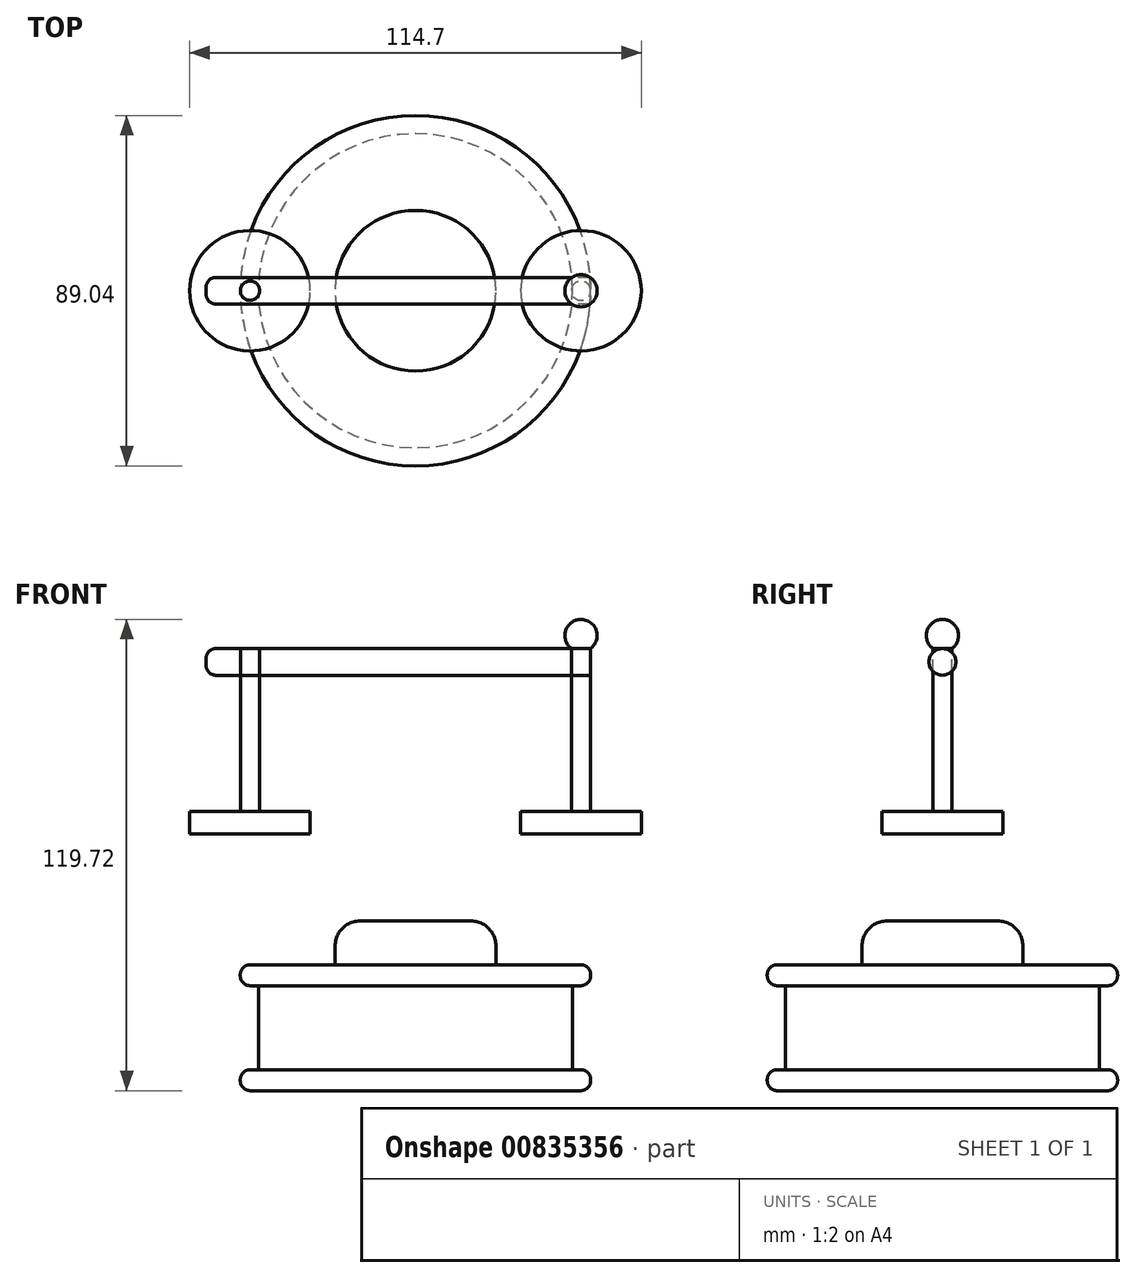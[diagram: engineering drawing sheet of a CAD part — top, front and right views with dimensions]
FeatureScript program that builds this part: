
annotation { "Feature Type Name" : "Feature", "Feature Type Description" : "" }
export const myFeature = defineFeature(function(context is Context, id is Id, definition is map)
    precondition{}
    {
        {
            var Q0;
            Q0=qCreatedBy(makeId("Front.planeOp"),FACE);
            var sketch = newSketch(context, id + "F0", { "sketchPlane" : qUnion([Q0])});
            skPoint(sketch, "E0.middle", {"position": v(0, -51.8) * mm});
            skLineSegment(sketch, "E1.bottom", {"start": v(41.98, -41.46) * mm, "end": v(-41.98, -41.46) * mm});
            skLineSegment(sketch, "E1.top", {"start": v(41.98, -36.1) * mm, "end": v(-41.98, -36.1) * mm});
            skLineSegment(sketch, "E1.left", {"start": v(44.52, -38.92) * mm, "end": v(44.52, -38.64) * mm});
            skLineSegment(sketch, "E1.right", {"start": v(-44.52, -38.92) * mm, "end": v(-44.52, -38.64) * mm});
            skPoint(sketch, "E1.middle", {"position": v(0, -38.78) * mm});
            skLineSegment(sketch, "E2.bottom", {"start": v(41.98, -68.12) * mm, "end": v(-41.98, -68.12) * mm});
            skLineSegment(sketch, "E2.top", {"start": v(41.98, -62.77) * mm, "end": v(-41.98, -62.77) * mm});
            skLineSegment(sketch, "E2.left", {"start": v(44.52, -65.58) * mm, "end": v(44.52, -65.31) * mm});
            skLineSegment(sketch, "E2.right", {"start": v(-44.52, -65.58) * mm, "end": v(-44.52, -65.31) * mm});
            skPoint(sketch, "E2.middle", {"position": v(0, -65.45) * mm});
            skLineSegment(sketch, "E3.bottom", {"start": v(20.42, -36.1) * mm, "end": v(-20.42, -36.1) * mm});
            skLineSegment(sketch, "E3.top", {"start": v(14.07, -25.01) * mm, "end": v(-14.07, -25.01) * mm});
            skLineSegment(sketch, "E3.left", {"start": v(20.42, -36.1) * mm, "end": v(20.42, -31.36) * mm});
            skLineSegment(sketch, "E3.right", {"start": v(-20.42, -36.1) * mm, "end": v(-20.42, -31.36) * mm});
            skPoint(sketch, "E3.middle", {"position": v(0, -30.56) * mm});
            skLineSegment(sketch, "E4.bottom", {"start": v(5.32, -25.01) * mm, "end": v(-5.32, -25.01) * mm});
            skLineSegment(sketch, "E4.top", {"start": v(5.32, 52.09) * mm, "end": v(-5.32, 52.09) * mm});
            skLineSegment(sketch, "E4.left", {"start": v(5.32, -25.01) * mm, "end": v(5.32, 52.09) * mm});
            skLineSegment(sketch, "E4.right", {"start": v(-5.32, -25.01) * mm, "end": v(-5.32, 52.09) * mm});
            skPoint(sketch, "E4.middle", {"position": v(0, 13.54) * mm});
            skArc(sketch, "E5", {"start": v(5.32, 52.09) * mm, "mid": v(0, 66.73) * mm, "end": v(-5.32, 52.09) * mm});
            skLineSegment(sketch, "E6.bottom", {"start": v(-5.32, 44.22) * mm, "end": v(-50.66, 44.22) * mm});
            skLineSegment(sketch, "E6.top", {"start": v(-5.32, 37.42) * mm, "end": v(-50.66, 37.42) * mm});
            skLineSegment(sketch, "E6.left", {"start": v(-5.32, 44.22) * mm, "end": v(-5.32, 37.42) * mm});
            skLineSegment(sketch, "E6.right", {"start": v(-53.2, 41.68) * mm, "end": v(-53.2, 39.96) * mm});
            skPoint(sketch, "E7.visualSharp", {"position": v(-44.52, -36.1) * mm});
            skArc(sketch, "E7.filletArc", {"start": v(-41.98, -36.1) * mm, "mid": v(-43.78, -36.85) * mm, "end": v(-44.52, -38.64) * mm});
            skPoint(sketch, "E8.visualSharp", {"position": v(-44.52, -41.46) * mm});
            skArc(sketch, "E8.filletArc", {"start": v(-44.52, -38.92) * mm, "mid": v(-43.78, -40.71) * mm, "end": v(-41.98, -41.46) * mm});
            skPoint(sketch, "E9.visualSharp", {"position": v(44.52, -36.1) * mm});
            skArc(sketch, "E9.filletArc", {"start": v(44.52, -38.64) * mm, "mid": v(43.78, -36.85) * mm, "end": v(41.98, -36.1) * mm});
            skPoint(sketch, "E10.visualSharp", {"position": v(44.52, -41.46) * mm});
            skArc(sketch, "E10.filletArc", {"start": v(41.98, -41.46) * mm, "mid": v(43.78, -40.71) * mm, "end": v(44.52, -38.92) * mm});
            skPoint(sketch, "E11.visualSharp", {"position": v(44.52, -62.77) * mm});
            skArc(sketch, "E11.filletArc", {"start": v(44.52, -65.31) * mm, "mid": v(43.78, -63.52) * mm, "end": v(41.98, -62.77) * mm});
            skPoint(sketch, "E12.visualSharp", {"position": v(44.52, -68.12) * mm});
            skArc(sketch, "E12.filletArc", {"start": v(41.98, -68.12) * mm, "mid": v(43.78, -67.38) * mm, "end": v(44.52, -65.58) * mm});
            skPoint(sketch, "E13.visualSharp", {"position": v(-44.52, -68.12) * mm});
            skArc(sketch, "E13.filletArc", {"start": v(-44.52, -65.58) * mm, "mid": v(-43.78, -67.38) * mm, "end": v(-41.98, -68.12) * mm});
            skPoint(sketch, "E14.visualSharp", {"position": v(-44.52, -62.77) * mm});
            skArc(sketch, "E14.filletArc", {"start": v(-41.98, -62.77) * mm, "mid": v(-43.78, -63.52) * mm, "end": v(-44.52, -65.31) * mm});
            skPoint(sketch, "E15.visualSharp", {"position": v(-53.2, 44.22) * mm});
            skArc(sketch, "E15.filletArc", {"start": v(-50.66, 44.22) * mm, "mid": v(-52.46, 43.48) * mm, "end": v(-53.2, 41.68) * mm});
            skPoint(sketch, "E16.visualSharp", {"position": v(-53.2, 37.42) * mm});
            skArc(sketch, "E16.filletArc", {"start": v(-53.2, 39.96) * mm, "mid": v(-52.46, 38.16) * mm, "end": v(-50.66, 37.42) * mm});
            skLineSegment(sketch, "E17.bottom", {"start": v(-44.5, 44.22) * mm, "end": v(-39.6, 44.22) * mm});
            skLineSegment(sketch, "E17.top", {"start": v(-44.5, 2.86) * mm, "end": v(-39.6, 2.86) * mm});
            skLineSegment(sketch, "E17.left", {"start": v(-44.5, 44.22) * mm, "end": v(-44.5, 2.86) * mm});
            skLineSegment(sketch, "E17.right", {"start": v(-39.6, 44.22) * mm, "end": v(-39.6, 2.86) * mm});
            skArc(sketch, "E18", {"start": v(-39.6, 44.22) * mm, "mid": v(-42.05, 51.6) * mm, "end": v(-44.5, 44.22) * mm});
            skLineSegment(sketch, "E19.bottom", {"start": v(-39.6, 2.86) * mm, "end": v(-44.5, 2.86) * mm});
            skLineSegment(sketch, "E19.top", {"start": v(-39.6, 2.86) * mm, "end": v(-44.5, 2.86) * mm});
            skLineSegment(sketch, "E19.left", {"start": v(-39.6, 2.86) * mm, "end": v(-39.6, 2.86) * mm});
            skLineSegment(sketch, "E19.right", {"start": v(-44.5, 2.86) * mm, "end": v(-44.5, 2.86) * mm});
            skPoint(sketch, "E19.middle", {"position": v(-42.05, 2.86) * mm});
            skLineSegment(sketch, "E20.bottom", {"start": v(-26.74, -2.83) * mm, "end": v(-57.35, -2.83) * mm});
            skLineSegment(sketch, "E20.top", {"start": v(-26.74, 2.83) * mm, "end": v(-57.35, 2.83) * mm});
            skLineSegment(sketch, "E20.left", {"start": v(-26.74, -2.83) * mm, "end": v(-26.74, 2.83) * mm});
            skLineSegment(sketch, "E20.right", {"start": v(-57.35, -2.83) * mm, "end": v(-57.35, 2.83) * mm});
            skPoint(sketch, "E20.middle", {"position": v(-42.05, 0) * mm});
            skLineSegment(sketch, "E21", {"start": v(0, -65.45) * mm, "end": v(0, 58.45) * mm});
            skLineSegment(sketch, "E22", {"start": v(0, -65.45) * mm, "end": v(0, -68.12) * mm});
            skLineSegment(sketch, "E23", {"start": v(0, 58.45) * mm, "end": v(0, 66.73) * mm});
            skLineSegment(sketch, "E24", {"start": v(-42.05, 0) * mm, "end": v(-42.05, 47.5) * mm});
            skLineSegment(sketch, "E25", {"start": v(-42.05, 0) * mm, "end": v(-42.05, -2.83) * mm});
            skLineSegment(sketch, "E26", {"start": v(-42.05, 47.5) * mm, "end": v(-42.05, 51.6) * mm});
            skArc(sketch, "E27.MirrorCS", {"start": v(39.6, 44.22) * mm, "mid": v(42.05, 51.6) * mm, "end": v(44.5, 44.22) * mm});
            skLineSegment(sketch, "E28.MirrorCS", {"start": v(5.32, 44.22) * mm, "end": v(50.66, 44.22) * mm});
            skLineSegment(sketch, "E29.MirrorCS", {"start": v(5.32, 37.42) * mm, "end": v(50.66, 37.42) * mm});
            skLineSegment(sketch, "E30.MirrorCS", {"start": v(39.6, 44.22) * mm, "end": v(39.6, 2.86) * mm});
            skLineSegment(sketch, "E31.MirrorCS", {"start": v(44.5, 44.22) * mm, "end": v(44.5, 2.86) * mm});
            skLineSegment(sketch, "E32.MirrorCS", {"start": v(26.74, 2.83) * mm, "end": v(57.35, 2.83) * mm});
            skLineSegment(sketch, "E33.MirrorCS", {"start": v(26.74, -2.83) * mm, "end": v(57.35, -2.83) * mm});
            skLineSegment(sketch, "E34.MirrorCS", {"start": v(57.35, -2.83) * mm, "end": v(57.35, 2.83) * mm});
            skLineSegment(sketch, "E35.MirrorCS", {"start": v(26.74, -2.83) * mm, "end": v(26.74, 2.83) * mm});
            skPoint(sketch, "E36.MirrorP", {"position": v(53.2, 44.22) * mm});
            skArc(sketch, "E37.MirrorCS", {"start": v(53.2, 39.96) * mm, "mid": v(52.46, 38.16) * mm, "end": v(50.66, 37.42) * mm});
            skLineSegment(sketch, "E38.MirrorCS", {"start": v(53.2, 41.68) * mm, "end": v(53.2, 39.96) * mm});
            skArc(sketch, "E39.MirrorCS", {"start": v(50.66, 44.22) * mm, "mid": v(52.46, 43.48) * mm, "end": v(53.2, 41.68) * mm});
            skPoint(sketch, "E40.visualSharp", {"position": v(-20.42, -25.01) * mm});
            skArc(sketch, "E40.filletArc", {"start": v(-14.07, -25.01) * mm, "mid": v(-18.56, -26.87) * mm, "end": v(-20.42, -31.36) * mm});
            skPoint(sketch, "E41.visualSharp", {"position": v(20.42, -25.01) * mm});
            skArc(sketch, "E41.filletArc", {"start": v(20.42, -31.36) * mm, "mid": v(18.56, -26.87) * mm, "end": v(14.07, -25.01) * mm});
            skLineSegment(sketch, "E42", {"start": v(0, 66.73) * mm, "end": v(0, -68.12) * mm});
            skLineSegment(sketch, "E43", {"start": v(-42.05, 51.6) * mm, "end": v(-42.05, -2.83) * mm});
            skLineSegment(sketch, "E44", {"start": v(-53.2, 40.82) * mm, "end": v(53.2, 40.82) * mm});
            skLineSegment(sketch, "E45", {"start": v(39.6, 2.86) * mm, "end": v(39.6, 2.83) * mm});
            skLineSegment(sketch, "E46", {"start": v(44.5, 2.86) * mm, "end": v(44.5, 2.83) * mm});
            skPoint(sketch, "E47.orphan", {"position": v(42.05, 0) * mm});
            skPoint(sketch, "E48.orphan", {"position": v(42.05, 51.6) * mm});
            skPoint(sketch, "E49.trimOffspring.end.orphan", {"position": v(42.05, -2.83) * mm});
            skLineSegment(sketch, "E50", {"start": v(42.05, 51.6) * mm, "end": v(42.05, -2.83) * mm});
            skLineSegment(sketch, "E51", {"start": v(5.32, 44.22) * mm, "end": v(-5.32, 44.22) * mm});
            skLineSegment(sketch, "E52", {"start": v(5.32, 37.42) * mm, "end": v(-5.32, 37.42) * mm});
            skPoint(sketch, "E53.MirrorCS.end.orphan", {"position": v(-57.35, -2.83) * mm});
            skPoint(sketch, "E53.MirrorCS.start.orphan", {"position": v(-26.74, -2.83) * mm});
            skPoint(sketch, "E54.orphan", {"position": v(-45.31, -62.14) * mm});
            skPoint(sketch, "E0.bottom.start.orphan", {"position": v(45.31, -62.14) * mm});
            skPoint(sketch, "E55.trimOffspring.end.orphan", {"position": v(-45.31, -41.46) * mm});
            skPoint(sketch, "E0.top.start.orphan", {"position": v(45.31, -41.46) * mm});
            skLineSegment(sketch, "E56.bottom", {"start": v(-39.91, -62.77) * mm, "end": v(39.91, -62.77) * mm});
            skLineSegment(sketch, "E56.left", {"start": v(-39.91, -62.77) * mm, "end": v(-39.91, -41.46) * mm});
            skLineSegment(sketch, "E56.right", {"start": v(39.91, -62.77) * mm, "end": v(39.91, -41.46) * mm});
            skPoint(sketch, "E57.orphan", {"position": v(39.91, -40.82) * mm});
            skPoint(sketch, "E58.orphan", {"position": v(-39.91, -40.82) * mm});
            skSolve(sketch);
        }
        {
            var Q0;
            {var subQ0=sQuery(id+"F0.wireOp",EDGE,"E5");var subQ3=sQuery(id+"F0.wireOp",EDGE,"E42");var subQ5=makeQuery(id+"F0.imprint","INTERSECT",VERTEX,{"derivedFrom":[subQ0,subQ3]});Q0=makeQuery(id+"F0.imprint","IMPRINT",FACE,{"disambiguationData":[TD([[makeQuery(id+"F0.imprint","IMPRINT",EDGE,{"disambiguationData":[TD([[subQ5,-1.0]])],"derivedFrom":subQ3}),-1.0]])]});}
            var Q1;
            {var subQ5=sQuery(id+"F0.wireOp",EDGE,"E3.right");Q1=makeQuery(id+"F0.imprint","IMPRINT",FACE,{"disambiguationData":[TD([[makeQuery(id+"F0.imprint","IMPRINT",EDGE,{"derivedFrom":subQ5}),-1.0]])]});}
            var Q2;
            Q2=makeQuery(id+"F0.imprint","IMPRINT",FACE,{"disambiguationData":[TD([[makeQuery(id+"F0.imprint","IMPRINT",EDGE,{"derivedFrom":sQuery(id+"F0.wireOp",EDGE,"E1.right")}),-1.0]])]});
            var Q3;
            {var subQ0=sQuery(id+"F0.wireOp",EDGE,"E0.right");Q3=makeQuery(id+"F0.imprint","IMPRINT",FACE,{"disambiguationData":[TD([[makeQuery(id+"F0.imprint","IMPRINT",EDGE,{"derivedFrom":subQ0}),-1.0]])]});}
            var Q4;
            Q4=makeQuery(id+"F0.imprint","IMPRINT",FACE,{"disambiguationData":[TD([[makeQuery(id+"F0.imprint","IMPRINT",EDGE,{"derivedFrom":sQuery(id+"F0.wireOp",EDGE,"E2.right")}),-1.0]])]});
            var Q5;
            {var subQ1=sQuery(id+"F0.wireOp",EDGE,"E4.bottom");var subQ3=sQuery(id+"F0.wireOp",EDGE,"E42");var subQ4=makeQuery(id+"F0.imprint","INTERSECT",VERTEX,{"derivedFrom":[subQ1,subQ3]});Q5=makeQuery(id+"F0.imprint","IMPRINT",FACE,{"disambiguationData":[TD([[makeQuery(id+"F0.imprint","IMPRINT",EDGE,{"disambiguationData":[TD([[subQ4,1.0]])],"derivedFrom":subQ3}),-1.0]])]});}
            var Q6;
            {var subQ3=sQuery(id+"F0.wireOp",EDGE,"E44");var subQ5=sQuery(id+"F0.wireOp",EDGE,"E42");var subQ7=makeQuery(id+"F0.imprint","INTERSECT",VERTEX,{"derivedFrom":[subQ5,subQ3]});Q6=makeQuery(id+"F0.imprint","IMPRINT",FACE,{"disambiguationData":[TD([[makeQuery(id+"F0.imprint","IMPRINT",EDGE,{"disambiguationData":[TD([[subQ7,-1.0]])],"derivedFrom":subQ5}),-1.0]])]});}
            var Q7;
            {var subQ0=sQuery(id+"F0.wireOp",EDGE,"E51");var subQ5=sQuery(id+"F0.wireOp",EDGE,"E42");var subQ7=makeQuery(id+"F0.imprint","INTERSECT",VERTEX,{"derivedFrom":[subQ5,subQ0]});Q7=makeQuery(id+"F0.imprint","IMPRINT",FACE,{"disambiguationData":[TD([[makeQuery(id+"F0.imprint","IMPRINT",EDGE,{"disambiguationData":[TD([[subQ7,-1.0]])],"derivedFrom":subQ5}),-1.0]])]});}
            var Q8;
            {var subQ1=sQuery(id+"F0.wireOp",EDGE,"E4.top");var subQ3=sQuery(id+"F0.wireOp",EDGE,"E42");var subQ4=makeQuery(id+"F0.imprint","INTERSECT",VERTEX,{"derivedFrom":[subQ1,subQ3]});Q8=makeQuery(id+"F0.imprint","IMPRINT",FACE,{"disambiguationData":[TD([[makeQuery(id+"F0.imprint","IMPRINT",EDGE,{"disambiguationData":[TD([[subQ4,-1.0]])],"derivedFrom":subQ3}),-1.0]])]});}
            var Q9;
            {var subQ5=sQuery(id+"F0.wireOp",EDGE,"E56.left");Q9=makeQuery(id+"F0.imprint","IMPRINT",FACE,{"disambiguationData":[TD([[makeQuery(id+"F0.imprint","IMPRINT",EDGE,{"derivedFrom":subQ5}),-1.0]])]});}
            var Q10;
            Q10=sQuery(id+"F0.wireOp",EDGE,"E42");
            revolve(context, id + "F1", {"surfaceOperationType" : NewSurfaceOperationType.NEW, "entities" : qUnion([Q0, Q1, Q2, Q3, Q4, Q5, Q6, Q7, Q8, Q9]), "axis" : qUnion([Q10]), "revolveType" : RevolveType.FULL});
        }
        {
            var Q0;
            {var subQ0=sQuery(id+"F0.wireOp",EDGE,"E6.left");var subQ5=sQuery(id+"F0.wireOp",EDGE,"E44");var subQ7=makeQuery(id+"F0.imprint","INTERSECT",VERTEX,{"derivedFrom":[subQ0,subQ5]});Q0=makeQuery(id+"F0.imprint","IMPRINT",FACE,{"disambiguationData":[TD([[makeQuery(id+"F0.imprint","IMPRINT",EDGE,{"disambiguationData":[TD([[subQ7,1.0]])],"derivedFrom":subQ5}),1.0]])]});}
            var Q1;
            {var subQ5=sQuery(id+"F0.wireOp",EDGE,"E15.filletArc");Q1=makeQuery(id+"F0.imprint","IMPRINT",FACE,{"disambiguationData":[TD([[makeQuery(id+"F0.imprint","IMPRINT",EDGE,{"derivedFrom":subQ5}),1.0]])]});}
            var Q2;
            {var subQ0=sQuery(id+"F0.wireOp",EDGE,"E28.MirrorCS");var subQ1=sQuery(id+"F0.wireOp",EDGE,"E4.left");var subQ2=makeQuery(id+"F0.imprint","INTERSECT",VERTEX,{"derivedFrom":[subQ1,subQ0]});Q2=makeQuery(id+"F0.imprint","IMPRINT",FACE,{"disambiguationData":[TD([[makeQuery(id+"F0.imprint","IMPRINT",EDGE,{"disambiguationData":[TD([[subQ2,1.0]])],"derivedFrom":subQ1}),-1.0]])]});}
            var Q3;
            {var subQ0=sQuery(id+"F0.wireOp",EDGE,"E39.MirrorCS");Q3=makeQuery(id+"F0.imprint","IMPRINT",FACE,{"disambiguationData":[TD([[makeQuery(id+"F0.imprint","IMPRINT",EDGE,{"derivedFrom":subQ0}),-1.0]])]});}
            var Q4;
            {var subQ0=sQuery(id+"F0.wireOp",EDGE,"E31.MirrorCS");var subQ5=sQuery(id+"F0.wireOp",EDGE,"E44");var subQ6=makeQuery(id+"F0.imprint","INTERSECT",VERTEX,{"derivedFrom":[subQ0,subQ5]});Q4=makeQuery(id+"F0.imprint","IMPRINT",FACE,{"disambiguationData":[TD([[makeQuery(id+"F0.imprint","IMPRINT",EDGE,{"disambiguationData":[TD([[subQ6,1.0]])],"derivedFrom":subQ5}),1.0]])]});}
            var Q5;
            {var subQ0=sQuery(id+"F0.wireOp",EDGE,"E30.MirrorCS");var subQ5=sQuery(id+"F0.wireOp",EDGE,"E44");var subQ6=makeQuery(id+"F0.imprint","INTERSECT",VERTEX,{"derivedFrom":[subQ0,subQ5]});Q5=makeQuery(id+"F0.imprint","IMPRINT",FACE,{"disambiguationData":[TD([[makeQuery(id+"F0.imprint","IMPRINT",EDGE,{"disambiguationData":[TD([[subQ6,-1.0]])],"derivedFrom":subQ5}),1.0]])]});}
            var Q6;
            {var subQ1=sQuery(id+"F0.wireOp",EDGE,"E17.bottom");var subQ3=sQuery(id+"F0.wireOp",EDGE,"E43");var subQ4=makeQuery(id+"F0.imprint","INTERSECT",VERTEX,{"derivedFrom":[subQ1,subQ3]});Q6=makeQuery(id+"F0.imprint","IMPRINT",FACE,{"disambiguationData":[TD([[makeQuery(id+"F0.imprint","IMPRINT",EDGE,{"disambiguationData":[TD([[subQ4,-1.0]])],"derivedFrom":subQ3}),-1.0]])]});}
            var Q7;
            {var subQ1=sQuery(id+"F0.wireOp",EDGE,"E17.bottom");var subQ3=sQuery(id+"F0.wireOp",EDGE,"E43");var subQ4=makeQuery(id+"F0.imprint","INTERSECT",VERTEX,{"derivedFrom":[subQ1,subQ3]});Q7=makeQuery(id+"F0.imprint","IMPRINT",FACE,{"disambiguationData":[TD([[makeQuery(id+"F0.imprint","IMPRINT",EDGE,{"disambiguationData":[TD([[subQ4,-1.0]])],"derivedFrom":subQ3}),1.0]])]});}
            var Q8;
            {var subQ0=sQuery(id+"F0.wireOp",EDGE,"E51");var subQ5=sQuery(id+"F0.wireOp",EDGE,"E42");var subQ6=makeQuery(id+"F0.imprint","INTERSECT",VERTEX,{"derivedFrom":[subQ5,subQ0]});Q8=makeQuery(id+"F0.imprint","IMPRINT",FACE,{"disambiguationData":[TD([[makeQuery(id+"F0.imprint","IMPRINT",EDGE,{"disambiguationData":[TD([[subQ6,-1.0]])],"derivedFrom":subQ5}),1.0]])]});}
            var Q9;
            {var subQ0=sQuery(id+"F0.wireOp",EDGE,"E51");var subQ5=sQuery(id+"F0.wireOp",EDGE,"E42");var subQ7=makeQuery(id+"F0.imprint","INTERSECT",VERTEX,{"derivedFrom":[subQ5,subQ0]});Q9=makeQuery(id+"F0.imprint","IMPRINT",FACE,{"disambiguationData":[TD([[makeQuery(id+"F0.imprint","IMPRINT",EDGE,{"disambiguationData":[TD([[subQ7,-1.0]])],"derivedFrom":subQ5}),-1.0]])]});}
            var Q10;
            Q10=sQuery(id+"F0.wireOp",EDGE,"E44");
            revolve(context, id + "F2", {"operationType" : NewBodyOperationType.ADD, "surfaceOperationType" : NewSurfaceOperationType.NEW, "entities" : qUnion([Q0, Q1, Q2, Q3, Q4, Q5, Q6, Q7, Q8, Q9]), "axis" : qUnion([Q10]), "revolveType" : RevolveType.FULL});
        }
        {
            var Q0;
            {var subQ0=sQuery(id+"F0.wireOp",EDGE,"E17.left");var subQ1=sQuery(id+"F0.wireOp",EDGE,"E6.top");var subQ2=makeQuery(id+"F0.imprint","INTERSECT",VERTEX,{"derivedFrom":[subQ1,subQ0]});Q0=makeQuery(id+"F0.imprint","IMPRINT",FACE,{"disambiguationData":[TD([[makeQuery(id+"F0.imprint","IMPRINT",EDGE,{"disambiguationData":[TD([[subQ2,1.0]])],"derivedFrom":subQ1}),1.0]])]});}
            var Q1;
            {var subQ0=sQuery(id+"F0.wireOp",EDGE,"E20.right");Q1=makeQuery(id+"F0.imprint","IMPRINT",FACE,{"disambiguationData":[TD([[makeQuery(id+"F0.imprint","IMPRINT",EDGE,{"derivedFrom":subQ0}),-1.0]])]});}
            var Q2;
            {var subQ0=sQuery(id+"F0.wireOp",EDGE,"E18");var subQ3=sQuery(id+"F0.wireOp",EDGE,"E43");var subQ5=makeQuery(id+"F0.imprint","INTERSECT",VERTEX,{"derivedFrom":[subQ0,subQ3]});Q2=makeQuery(id+"F0.imprint","IMPRINT",FACE,{"disambiguationData":[TD([[makeQuery(id+"F0.imprint","IMPRINT",EDGE,{"disambiguationData":[TD([[subQ5,-1.0]])],"derivedFrom":subQ3}),-1.0]])]});}
            var Q3;
            {var subQ1=sQuery(id+"F0.wireOp",EDGE,"E17.bottom");var subQ3=sQuery(id+"F0.wireOp",EDGE,"E43");var subQ4=makeQuery(id+"F0.imprint","INTERSECT",VERTEX,{"derivedFrom":[subQ1,subQ3]});Q3=makeQuery(id+"F0.imprint","IMPRINT",FACE,{"disambiguationData":[TD([[makeQuery(id+"F0.imprint","IMPRINT",EDGE,{"disambiguationData":[TD([[subQ4,-1.0]])],"derivedFrom":subQ3}),-1.0]])]});}
            var Q4;
            {var subQ0=sQuery(id+"F0.wireOp",EDGE,"E17.left");var subQ1=sQuery(id+"F0.wireOp",EDGE,"E6.top");var subQ2=makeQuery(id+"F0.imprint","INTERSECT",VERTEX,{"derivedFrom":[subQ1,subQ0]});Q4=makeQuery(id+"F0.imprint","IMPRINT",FACE,{"disambiguationData":[TD([[makeQuery(id+"F0.imprint","IMPRINT",EDGE,{"disambiguationData":[TD([[subQ2,1.0]])],"derivedFrom":subQ1}),-1.0]])]});}
            var Q5;
            {var subQ0=sQuery(id+"F0.wireOp",EDGE,"E19.top");var subQ1=sQuery(id+"F0.wireOp",EDGE,"E17.left");var subQ2=makeQuery(id+"F0.imprint","INTERSECT",VERTEX,{"derivedFrom":[subQ1,subQ0]});Q5=makeQuery(id+"F0.imprint","IMPRINT",FACE,{"disambiguationData":[TD([[makeQuery(id+"F0.imprint","IMPRINT",EDGE,{"disambiguationData":[TD([[subQ2,1.0]])],"derivedFrom":subQ1}),1.0]])]});}
            var Q6;
            Q6=sQuery(id+"F0.wireOp",EDGE,"E43");
            revolve(context, id + "F3", {"surfaceOperationType" : NewSurfaceOperationType.NEW, "entities" : qUnion([Q0, Q1, Q2, Q3, Q4, Q5]), "axis" : qUnion([Q6]), "revolveType" : RevolveType.FULL});
        }
        {
            var Q0;
            {var subQ1=sQuery(id+"F0.wireOp",EDGE,"E27.MirrorCS");var subQ3=sQuery(id+"F0.wireOp",EDGE,"E50");var subQ4=makeQuery(id+"F0.imprint","INTERSECT",VERTEX,{"derivedFrom":[subQ1,subQ3]});Q0=makeQuery(id+"F0.imprint","IMPRINT",FACE,{"disambiguationData":[TD([[makeQuery(id+"F0.imprint","IMPRINT",EDGE,{"disambiguationData":[TD([[subQ4,-1.0]])],"derivedFrom":subQ3}),-1.0]])]});}
            var Q1;
            {var subQ0=sQuery(id+"F0.wireOp",EDGE,"E30.MirrorCS");var subQ5=sQuery(id+"F0.wireOp",EDGE,"E44");var subQ6=makeQuery(id+"F0.imprint","INTERSECT",VERTEX,{"derivedFrom":[subQ0,subQ5]});Q1=makeQuery(id+"F0.imprint","IMPRINT",FACE,{"disambiguationData":[TD([[makeQuery(id+"F0.imprint","IMPRINT",EDGE,{"disambiguationData":[TD([[subQ6,-1.0]])],"derivedFrom":subQ5}),1.0]])]});}
            var Q2;
            {var subQ0=sQuery(id+"F0.wireOp",EDGE,"E30.MirrorCS");var subQ1=sQuery(id+"F0.wireOp",EDGE,"E29.MirrorCS");var subQ2=makeQuery(id+"F0.imprint","INTERSECT",VERTEX,{"derivedFrom":[subQ1,subQ0]});Q2=makeQuery(id+"F0.imprint","IMPRINT",FACE,{"disambiguationData":[TD([[makeQuery(id+"F0.imprint","IMPRINT",EDGE,{"disambiguationData":[TD([[subQ2,-1.0]])],"derivedFrom":subQ1}),1.0]])]});}
            var Q3;
            {var subQ0=sQuery(id+"F0.wireOp",EDGE,"E45");Q3=makeQuery(id+"F0.imprint","IMPRINT",FACE,{"disambiguationData":[TD([[makeQuery(id+"F0.imprint","IMPRINT",EDGE,{"derivedFrom":subQ0}),1.0]])]});}
            var Q4;
            {var subQ0=sQuery(id+"F0.wireOp",EDGE,"E35.MirrorCS");Q4=makeQuery(id+"F0.imprint","IMPRINT",FACE,{"disambiguationData":[TD([[makeQuery(id+"F0.imprint","IMPRINT",EDGE,{"derivedFrom":subQ0}),-1.0]])]});}
            var Q5;
            {var subQ1=sQuery(id+"F0.wireOp",EDGE,"E29.MirrorCS");var subQ3=sQuery(id+"F0.wireOp",EDGE,"E30.MirrorCS");var subQ4=makeQuery(id+"F0.imprint","INTERSECT",VERTEX,{"derivedFrom":[subQ1,subQ3]});Q5=makeQuery(id+"F0.imprint","IMPRINT",FACE,{"disambiguationData":[TD([[makeQuery(id+"F0.imprint","IMPRINT",EDGE,{"disambiguationData":[TD([[subQ4,-1.0]])],"derivedFrom":subQ3}),1.0]])]});}
            var Q6;
            Q6=sQuery(id+"F0.wireOp",EDGE,"E50");
            revolve(context, id + "F4", {"surfaceOperationType" : NewSurfaceOperationType.NEW, "entities" : qUnion([Q0, Q1, Q2, Q3, Q4, Q5]), "axis" : qUnion([Q6]), "revolveType" : RevolveType.FULL});
        }
    });
